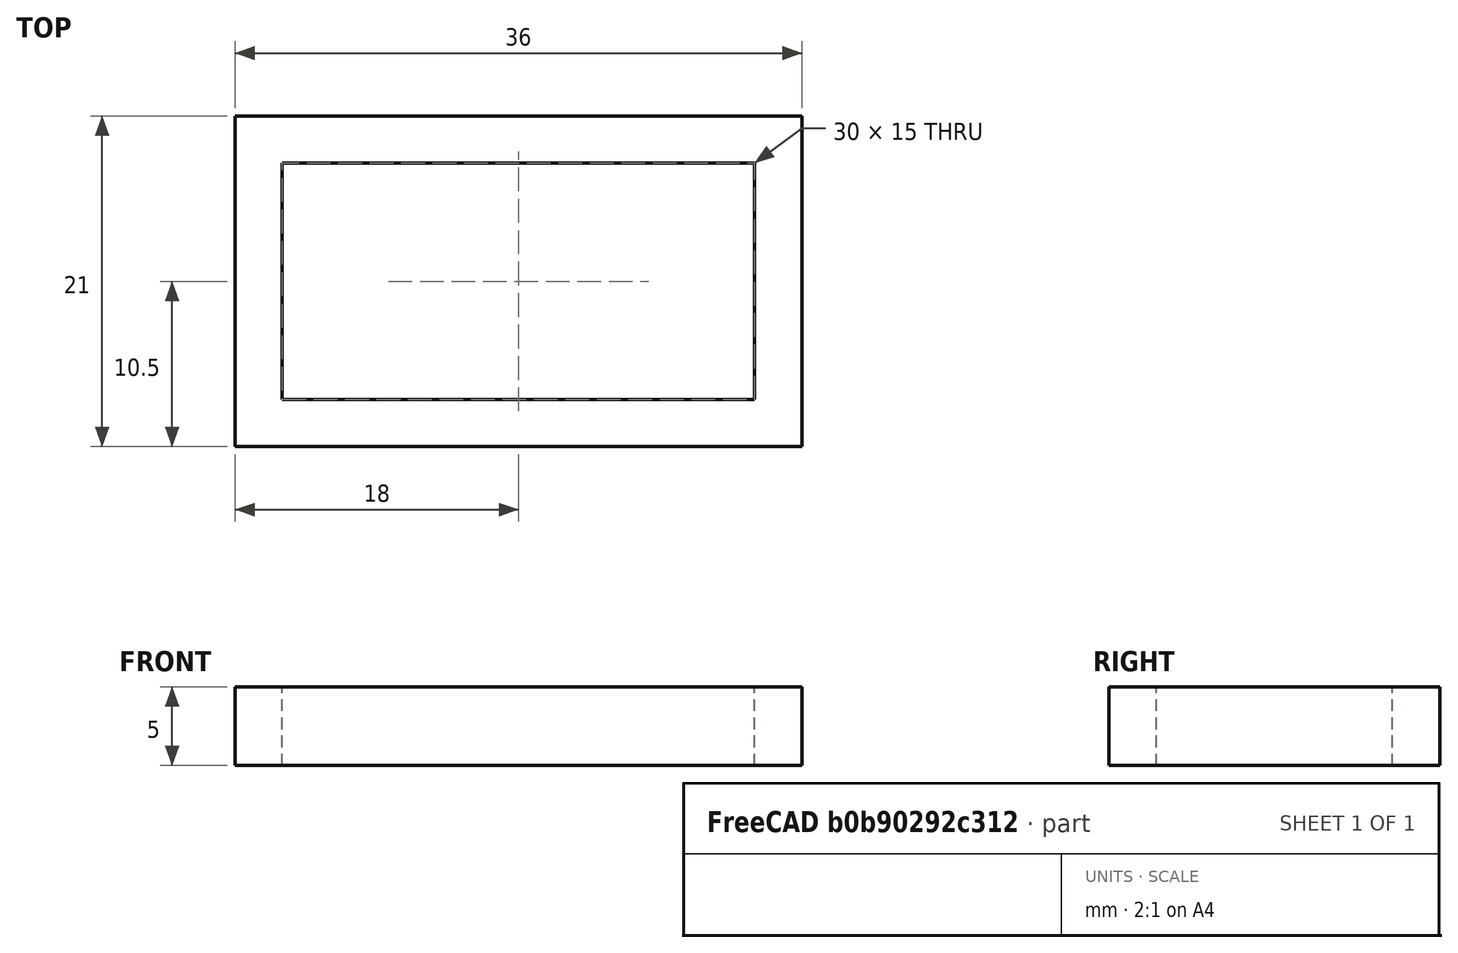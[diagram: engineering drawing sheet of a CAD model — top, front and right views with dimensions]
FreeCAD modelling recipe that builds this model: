
FCSTD DOCUMENT  (FreeCAD 0.16R6706 (Git))
Label: Theremin_Ventana_V1
License: All rights reserved
LicenseURL: http://en.wikipedia.org/wiki/All_rights_reserved
objects: Sketcher::SketchObject×1, PartDesign::Pad×1
note: 3 computed .brp shape members not serialized (recipe doc carries the construction recipe); baked Part::Feature solids carry a one-line shape summary decoded from their .brp

FEATURE [Sketcher::SketchObject] Sketch
  sketch-geometry (8):
    g0: LineSegment StartX=0 StartY=15 StartZ=0 EndX=30 EndY=15 EndZ=0
    g1: LineSegment StartX=30 StartY=15 StartZ=0 EndX=30 EndY=0 EndZ=0
    g2: LineSegment StartX=30 StartY=0 StartZ=0 EndX=0 EndY=0 EndZ=0
    g3: LineSegment StartX=0 StartY=0 StartZ=0 EndX=0 EndY=15 EndZ=0
    g4: LineSegment StartX=-3 StartY=18 StartZ=0 EndX=33 EndY=18 EndZ=0
    g5: LineSegment StartX=33 StartY=18 StartZ=0 EndX=33 EndY=-3 EndZ=0
    g6: LineSegment StartX=33 StartY=-3 StartZ=0 EndX=-3 EndY=-3 EndZ=0
    g7: LineSegment StartX=-3 StartY=-3 StartZ=0 EndX=-3 EndY=18 EndZ=0
  constraints (23):
    c: Coincident(g0,g1)
    c: Coincident(g1,g2)
    c: Coincident(g2,g3)
    c: Coincident(g3,g0)
    c: Horizontal(g0)
    c: Horizontal(g2)
    c: Vertical(g1)
    c: Vertical(g3)
    c: DistanceX(g0,g0) = 30
    c: DistanceY(g1,g1) = 15
    c: Coincident(g2,g-1)
    c: Coincident(g4,g5)
    c: Coincident(g5,g6)
    c: Coincident(g6,g7)
    c: Coincident(g7,g4)
    c: Horizontal(g4)
    c: Horizontal(g6)
    c: Vertical(g5)
    c: Vertical(g7)
    c: DistanceX(g6,g6) = 36
    c: DistanceY(g7,g7) = 21
    c: DistanceY(g6,g-1) = 3
    c: DistanceX(g6,g-1) = 3
FEATURE [PartDesign::Pad] Pad
  Length = 5
  Length2 = 100
  Sketch = -> Sketch
  Type = 0
